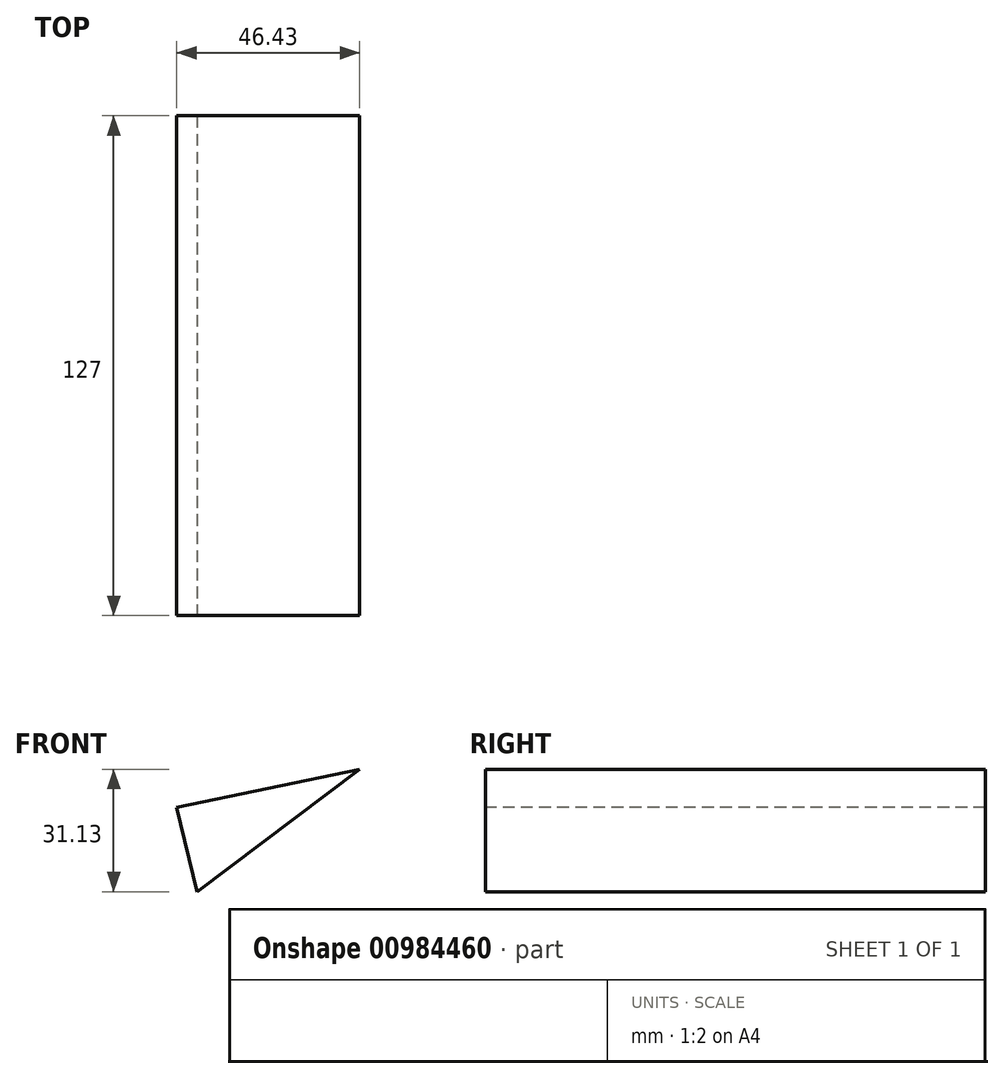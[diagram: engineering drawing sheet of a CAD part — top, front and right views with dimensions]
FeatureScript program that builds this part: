
annotation { "Feature Type Name" : "Feature", "Feature Type Description" : "" }
export const myFeature = defineFeature(function(context is Context, id is Id, definition is map)
    precondition{}
    {
        {
            var Q0;
            Q0=qCreatedBy(makeId("Front.planeOp"),FACE);
            var sketch = newSketch(context, id + "F0", { "sketchPlane" : qUnion([Q0])});
            skLineSegment(sketch, "E0", {"start": v(-16.08, -33.03) * mm, "end": v(30.35, -23.27) * mm});
            skLineSegment(sketch, "E1", {"start": v(30.35, -23.27) * mm, "end": v(-10.9, -54.4) * mm});
            skLineSegment(sketch, "E2", {"start": v(-10.9, -54.4) * mm, "end": v(-16.08, -33.03) * mm});
            skSolve(sketch);
        }
        {
            var Q0;
            Q0=makeQuery(id+"F0.imprint","IMPRINT",FACE,{"disambiguationData":[TD([[makeQuery(id+"F0.imprint","IMPRINT",EDGE,{"derivedFrom":sQuery(id+"F0.wireOp",EDGE,"E0")}),-1.0]])]});
            var sketch = newSketch(context, id + "F1", { "sketchPlane" : qUnion([Q0])});
            skSolve(sketch);
        }
        {
            var Q0;
            Q0=makeQuery(id+"F1.imprint","IMPRINT",FACE,{"disambiguationData":[TD([[makeQuery(id+"F1.imprint","IMPRINT",EDGE,{"derivedFrom":makeQuery(id+"F0.imprint","IMPRINT",EDGE,{"derivedFrom":sQuery(id+"F0.wireOp",EDGE,"E0")})}),-1.0]])]});
            extrude(context, id + "F2", {"entities" : qUnion([Q0]), "oppositeDirection" : true, "depth" : 127 * mm, "offsetDistance" : 25.4 * mm});
        }
    });
